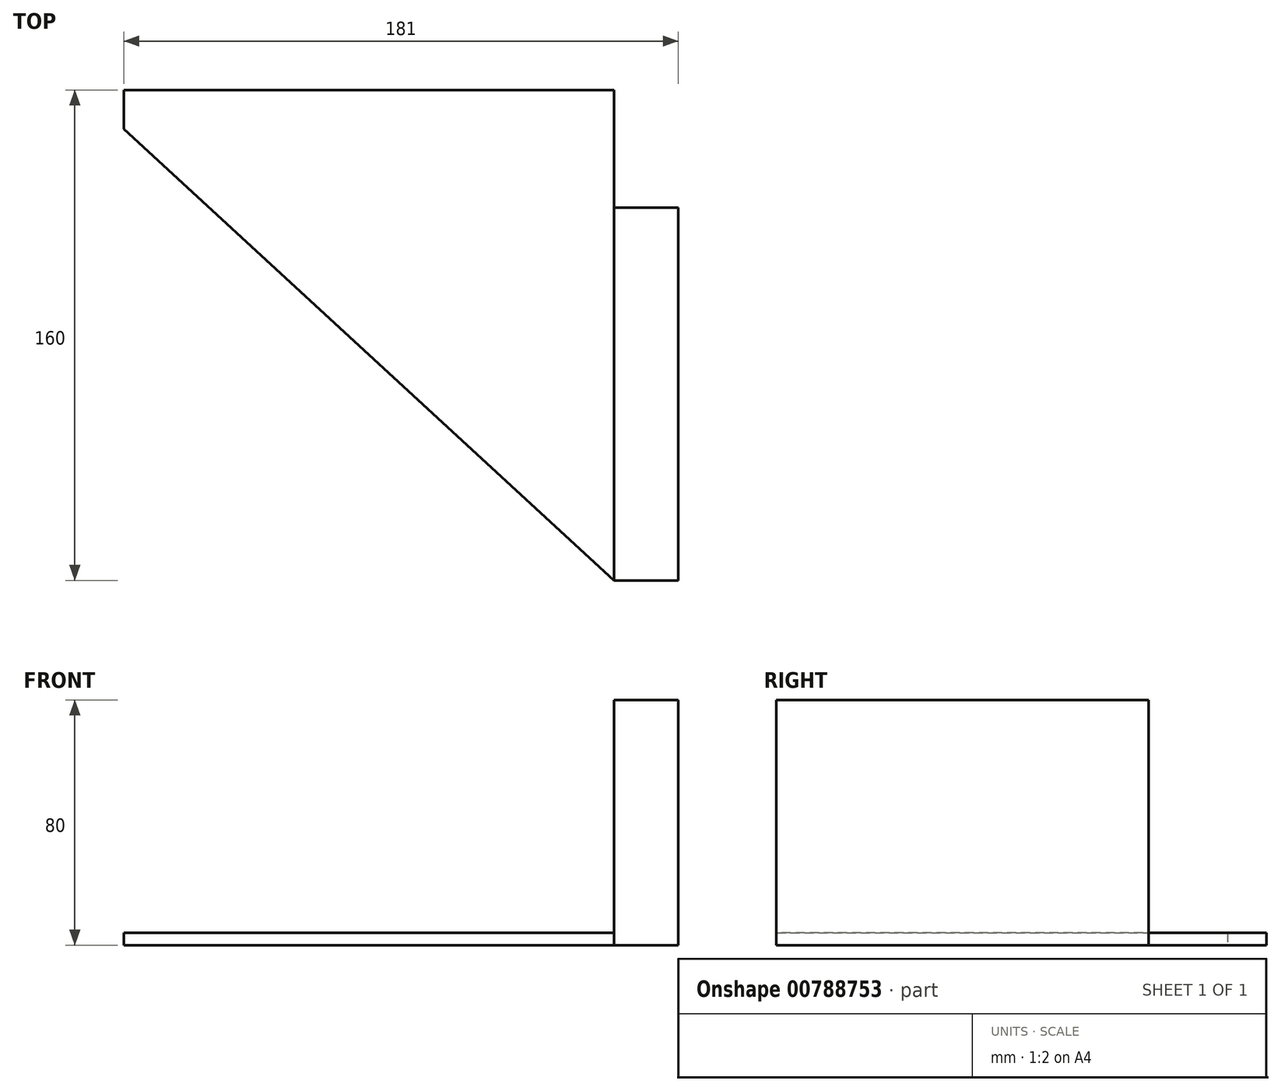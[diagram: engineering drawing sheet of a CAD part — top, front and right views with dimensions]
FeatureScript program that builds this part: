
annotation { "Feature Type Name" : "Feature", "Feature Type Description" : "" }
export const myFeature = defineFeature(function(context is Context, id is Id, definition is map)
    precondition{}
    {
        {
            var Q0;
            Q0=qCreatedBy(makeId("Top.planeOp"),FACE);
            var sketch = newSketch(context, id + "F0", { "sketchPlane" : qUnion([Q0])});
            skLineSegment(sketch, "E0.bottom", {"start": v(0, 0) * mm, "end": v(160, 0) * mm});
            skLineSegment(sketch, "E0.top", {"start": v(0, 160) * mm, "end": v(160, 160) * mm});
            skLineSegment(sketch, "E0.left", {"start": v(0, 0) * mm, "end": v(0, 160) * mm});
            skLineSegment(sketch, "E0.right", {"start": v(160, 0) * mm, "end": v(160, 160) * mm});
            skLineSegment(sketch, "E1", {"start": v(0, 155) * mm, "end": v(160, 155) * mm, "construction": true});
            skLineSegment(sketch, "E2.bottom", {"start": v(160, 0) * mm, "end": v(181, 0) * mm});
            skLineSegment(sketch, "E2.top", {"start": v(160, 121.59) * mm, "end": v(181, 121.59) * mm});
            skLineSegment(sketch, "E2.left", {"start": v(160, 0) * mm, "end": v(160, 121.59) * mm});
            skLineSegment(sketch, "E2.right", {"start": v(181, 0) * mm, "end": v(181, 121.59) * mm});
            skLineSegment(sketch, "E3", {"start": v(0, 147.3) * mm, "end": v(160, 0) * mm});
            skSolve(sketch);
        }
        {
            var Q0;
            {var subQ1=sQuery(id+"F0.wireOp",EDGE,"E0.top");Q0=makeQuery(id+"F0.imprint","IMPRINT",FACE,{"disambiguationData":[TD([[makeQuery(id+"F0.imprint","IMPRINT",EDGE,{"derivedFrom":subQ1}),-1.0]])]});}
            extrude(context, id + "F1", {"entities" : qUnion([Q0]), "depth" : 4 * mm, "offsetDistance" : 25 * mm});
        }
        {
            var Q0;
            Q0=makeQuery(id+"F0.imprint","IMPRINT",FACE,{"disambiguationData":[TD([[makeQuery(id+"F0.imprint","IMPRINT",EDGE,{"derivedFrom":sQuery(id+"F0.wireOp",EDGE,"E2.bottom")}),1.0]])]});
            extrude(context, id + "F2", {"entities" : qUnion([Q0]), "operationType" : NewBodyOperationType.ADD, "depth" : 80 * mm, "offsetDistance" : 25 * mm});
        }
    });
